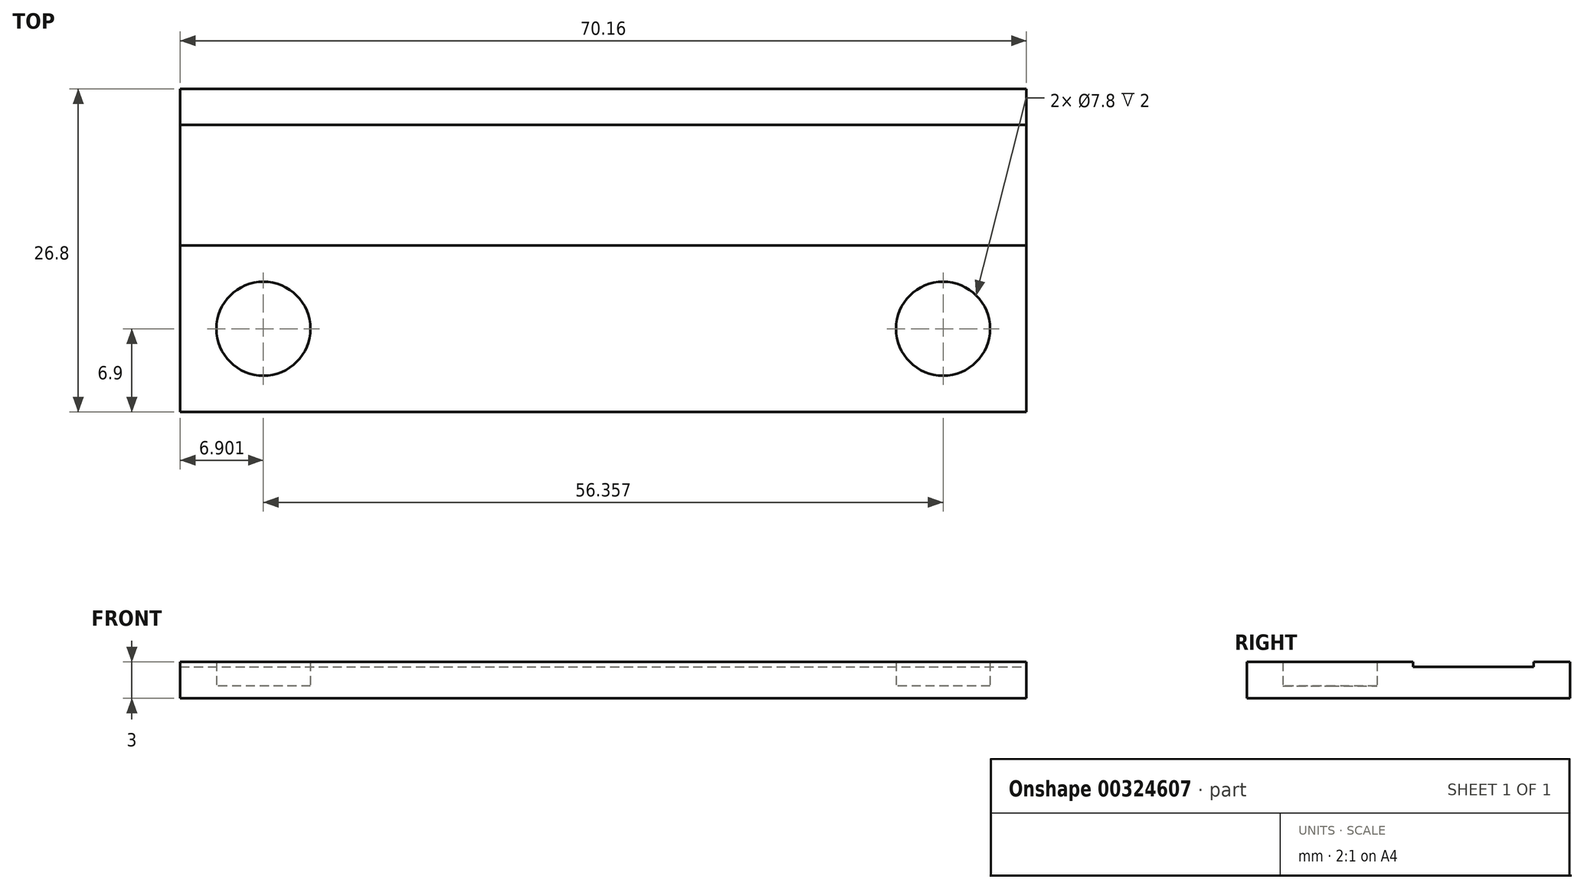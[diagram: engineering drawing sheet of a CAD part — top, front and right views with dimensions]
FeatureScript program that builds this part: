
annotation { "Feature Type Name" : "Feature", "Feature Type Description" : "" }
export const myFeature = defineFeature(function(context is Context, id is Id, definition is map)
    precondition{}
    {
        {
            var Q0;
            Q0=qCreatedBy(makeId("Top.planeOp"),FACE);
            var sketch = newSketch(context, id + "F0", { "sketchPlane" : qUnion([Q0])});
            skLineSegment(sketch, "E0.bottom", {"start": v(-35.08, 6.9) * mm, "end": v(35.08, 6.9) * mm});
            skLineSegment(sketch, "E0.top", {"start": v(-35.08, -6.9) * mm, "end": v(35.08, -6.9) * mm});
            skLineSegment(sketch, "E0.left", {"start": v(-35.08, 6.9) * mm, "end": v(-35.08, -6.9) * mm});
            skLineSegment(sketch, "E0.right", {"start": v(35.08, 6.9) * mm, "end": v(35.08, -6.9) * mm});
            skPoint(sketch, "E0.middle", {"position": v(0, 0) * mm});
            skCircle(sketch, "E1", {"center": v(-28.18, 0) * mm, "radius": 3.9 * mm});
            skLineSegment(sketch, "E2", {"start": v(-35.08, 6.9) * mm, "end": v(-35.08, 16.9) * mm});
            skLineSegment(sketch, "E3", {"start": v(-35.08, 16.9) * mm, "end": v(35.08, 16.9) * mm});
            skLineSegment(sketch, "E4", {"start": v(35.08, 16.9) * mm, "end": v(35.08, 6.9) * mm});
            skLineSegment(sketch, "E5", {"start": v(-35.08, 16.9) * mm, "end": v(-35.08, 19.9) * mm});
            skLineSegment(sketch, "E6", {"start": v(-35.08, 19.9) * mm, "end": v(35.08, 19.9) * mm});
            skLineSegment(sketch, "E7", {"start": v(35.08, 19.9) * mm, "end": v(35.08, 16.9) * mm});
            skCircle(sketch, "E8.MirrorC", {"center": v(28.18, 0) * mm, "radius": 3.9 * mm});
            skSolve(sketch);
        }
        {
            var Q0;
            Q0=qCreatedBy(makeId("Top.planeOp"),FACE);
            var sketch = newSketch(context, id + "F1", { "sketchPlane" : qUnion([Q0])});
            skLineSegment(sketch, "E9.0", {"start": v(-35.08, 19.9) * mm, "end": v(35.08, 19.9) * mm});
            skLineSegment(sketch, "E9.1", {"start": v(-35.08, -6.9) * mm, "end": v(35.08, -6.9) * mm});
            skLineSegment(sketch, "E10", {"start": v(-35.08, -6.9) * mm, "end": v(-35.08, 19.9) * mm});
            skLineSegment(sketch, "E11", {"start": v(35.08, 19.9) * mm, "end": v(35.08, -6.9) * mm});
            skSolve(sketch);
        }
        {
            var Q0;
            Q0=makeQuery(id+"F1.imprint","IMPRINT",FACE,{"disambiguationData":[TD([[makeQuery(id+"F1.imprint","IMPRINT",EDGE,{"derivedFrom":sQuery(id+"F1.wireOp",EDGE,"E9.0")}),-1.0]])]});
            extrude(context, id + "F2", {"entities" : qUnion([Q0]), "oppositeDirection" : true, "depth" : 1 * mm, "offsetDistance" : 25 * mm});
        }
        {
            var Q0;
            Q0=makeQuery(id+"F0.imprint","IMPRINT",FACE,{"disambiguationData":[TD([[makeQuery(id+"F0.imprint","IMPRINT",EDGE,{"derivedFrom":sQuery(id+"F0.wireOp",EDGE,"E0.bottom")}),-1.0]])]});
            var Q1;
            Q1=makeQuery(id+"F0.imprint","IMPRINT",FACE,{"disambiguationData":[TD([[makeQuery(id+"F0.imprint","IMPRINT",EDGE,{"derivedFrom":sQuery(id+"F0.wireOp",EDGE,"E3")}),1.0]])]});
            extrude(context, id + "F3", {"entities" : qUnion([Q0, Q1]), "operationType" : NewBodyOperationType.ADD, "depth" : 2 * mm, "offsetDistance" : 25 * mm});
        }
        {
            var Q0;
            Q0=makeQuery(id+"F0.imprint","IMPRINT",FACE,{"disambiguationData":[TD([[makeQuery(id+"F0.imprint","IMPRINT",EDGE,{"derivedFrom":sQuery(id+"F0.wireOp",EDGE,"E0.bottom")}),1.0]])]});
            extrude(context, id + "F4", {"entities" : qUnion([Q0]), "operationType" : NewBodyOperationType.ADD, "depth" : 1.6 * mm, "offsetDistance" : 25 * mm});
        }
    });
